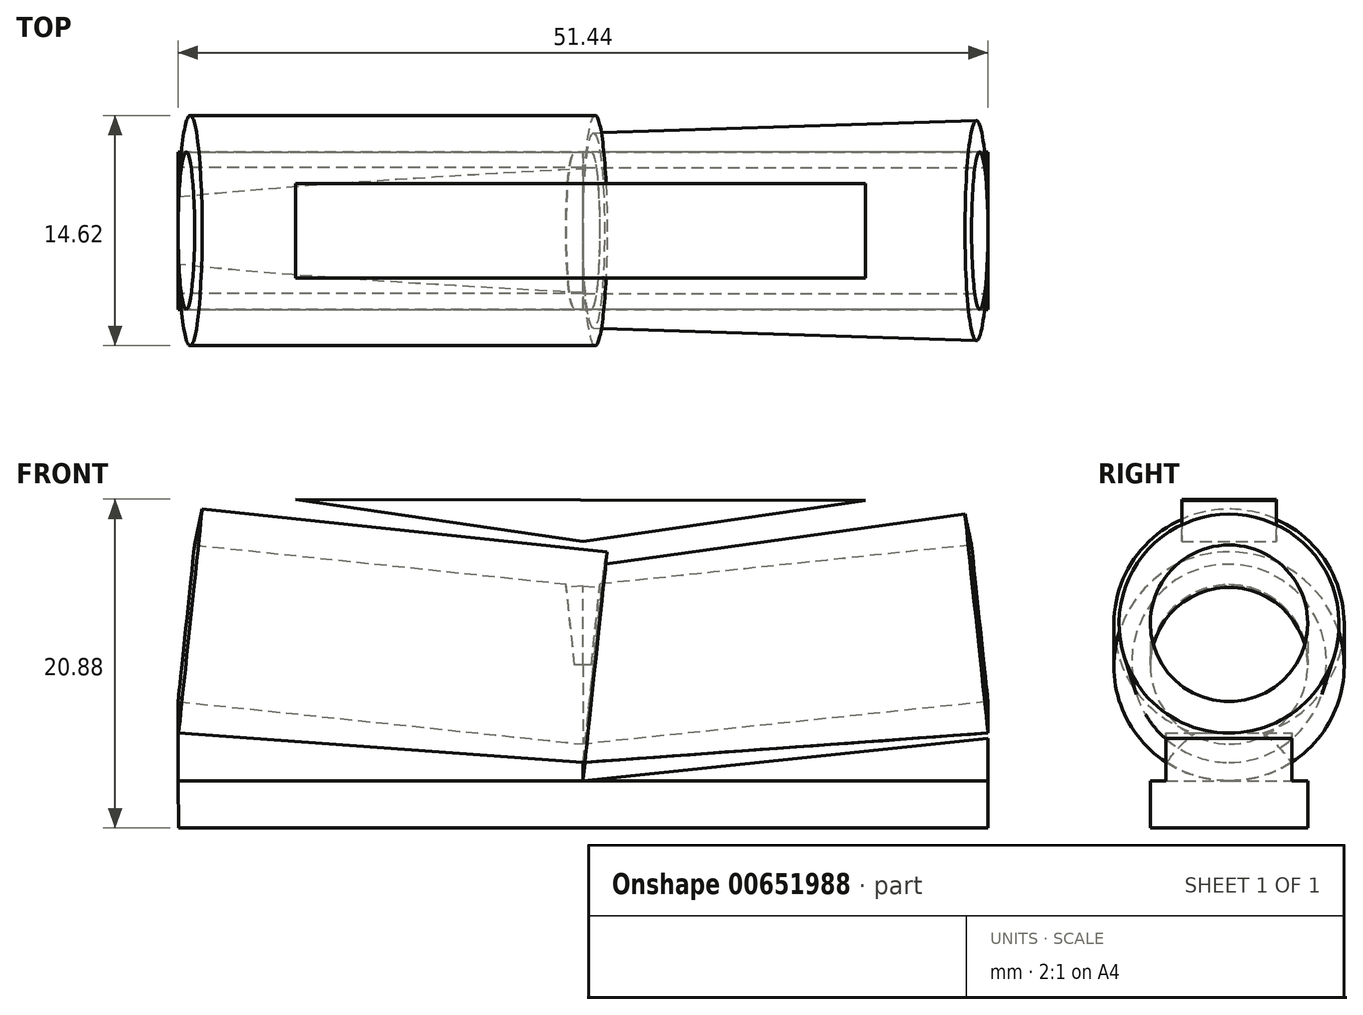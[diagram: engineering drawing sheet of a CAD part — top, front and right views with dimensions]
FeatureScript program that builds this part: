
annotation { "Feature Type Name" : "Feature", "Feature Type Description" : "" }
export const myFeature = defineFeature(function(context is Context, id is Id, definition is map)
    precondition{}
    {
        {
            var Q0;
            Q0=qCreatedBy(makeId("Front.planeOp"),FACE);
            var sketch = newSketch(context, id + "F0", { "sketchPlane" : qUnion([Q0])});
            skLineSegment(sketch, "E0", {"start": v(0, 0) * mm, "end": v(25.72, 0) * mm});
            skLineSegment(sketch, "E1", {"start": v(0, 0) * mm, "end": v(25.72, 2.7) * mm});
            skLineSegment(sketch, "E2", {"start": v(25.72, 2.7) * mm, "end": v(0, 0) * mm});
            skLineSegment(sketch, "E3", {"start": v(0, 2.32) * mm, "end": v(25.72, 5.03) * mm});
            skLineSegment(sketch, "E4", {"start": v(0, 0) * mm, "end": v(0, 2.32) * mm});
            skLineSegment(sketch, "E5", {"start": v(0, 7.35) * mm, "end": v(25.72, 10.06) * mm});
            skLineSegment(sketch, "E6", {"start": v(0, 2.32) * mm, "end": v(0, 7.35) * mm});
            skPoint(sketch, "E7", {"position": v(0, 2.32) * mm});
            skLineSegment(sketch, "E8", {"start": v(25.72, 10.06) * mm, "end": v(25.72, 0) * mm});
            skPoint(sketch, "E9", {"position": v(0, 0) * mm});
            skLineSegment(sketch, "E10.MirrorCS", {"start": v(0, 7.35) * mm, "end": v(-25.72, 10.06) * mm});
            skLineSegment(sketch, "E11.MirrorCS", {"start": v(0, 2.32) * mm, "end": v(-25.72, 5.03) * mm});
            skLineSegment(sketch, "E12.MirrorCS", {"start": v(-25.72, 2.7) * mm, "end": v(0, 0) * mm});
            skLineSegment(sketch, "E13.MirrorCS", {"start": v(0, 0) * mm, "end": v(-25.72, 0) * mm});
            skLineSegment(sketch, "E14.MirrorCS", {"start": v(-25.72, 10.06) * mm, "end": v(-25.72, 0) * mm});
            skLineSegment(sketch, "E15", {"start": v(25.72, 0) * mm, "end": v(25.72, -3) * mm});
            skLineSegment(sketch, "E16", {"start": v(25.72, -3) * mm, "end": v(-25.7, -3) * mm});
            skLineSegment(sketch, "E17", {"start": v(-25.7, -3) * mm, "end": v(-25.72, 0) * mm});
            skPoint(sketch, "E18", {"position": v(-25.72, 5.03) * mm});
            skPoint(sketch, "E19", {"position": v(-25.72, 2.7) * mm});
            skPoint(sketch, "E20", {"position": v(-25.72, 0) * mm});
            skPoint(sketch, "E21", {"position": v(25.72, 0) * mm});
            skPoint(sketch, "E22", {"position": v(25.72, 2.7) * mm});
            skPoint(sketch, "E23", {"position": v(25.72, 5.03) * mm});
            skPoint(sketch, "E24", {"position": v(0, 1.16) * mm});
            skPoint(sketch, "E25", {"position": v(-25.72, 3.03) * mm});
            skLineSegment(sketch, "E26", {"start": v(0, 1.16) * mm, "end": v(-25.72, 3.03) * mm});
            skPoint(sketch, "E27", {"position": v(25.72, 3.03) * mm});
            skLineSegment(sketch, "E28", {"start": v(25.72, 3.03) * mm, "end": v(0, 1.16) * mm});
            skSolve(sketch);
        }
        {
            var Q0;
            {var subQ0=sQuery(id+"F0.wireOp",EDGE,"E11.MirrorCS");Q0=makeQuery(id+"F0.imprint","IMPRINT",FACE,{"disambiguationData":[TD([[makeQuery(id+"F0.imprint","IMPRINT",EDGE,{"derivedFrom":subQ0}),1.0]])]});}
            var Q1;
            {var subQ0=sQuery(id+"F0.wireOp",EDGE,"E12.MirrorCS");Q1=makeQuery(id+"F0.imprint","IMPRINT",FACE,{"disambiguationData":[TD([[makeQuery(id+"F0.imprint","IMPRINT",EDGE,{"derivedFrom":subQ0}),1.0]])]});}
            var Q2;
            Q2=sQuery(id+"F0.wireOp",EDGE,"E10.MirrorCS");
            revolve(context, id + "F1", {"entities" : qUnion([Q0, Q1]), "axis" : qUnion([Q2]), "revolveType" : RevolveType.FULL});
        }
        {
            var Q0;
            {var subQ0=sQuery(id+"F0.wireOp",EDGE,"E2");Q0=makeQuery(id+"F0.imprint","IMPRINT",FACE,{"disambiguationData":[TD([[makeQuery(id+"F0.imprint","IMPRINT",EDGE,{"derivedFrom":subQ0}),-1.0]])]});}
            var Q1;
            {var subQ0=sQuery(id+"F0.wireOp",EDGE,"E3");Q1=makeQuery(id+"F0.imprint","IMPRINT",FACE,{"disambiguationData":[TD([[makeQuery(id+"F0.imprint","IMPRINT",EDGE,{"derivedFrom":subQ0}),-1.0]])]});}
            var Q2;
            Q2=sQuery(id+"F0.wireOp",EDGE,"E5");
            revolve(context, id + "F2", {"operationType" : NewBodyOperationType.ADD, "entities" : qUnion([Q0, Q1]), "axis" : qUnion([Q2]), "revolveType" : RevolveType.FULL});
        }
        {
            var Q0;
            Q0=qCreatedBy(makeId("Front.planeOp"),FACE);
            var sketch = newSketch(context, id + "F3", { "sketchPlane" : qUnion([Q0])});
            skPoint(sketch, "E29", {"position": v(0, 15.2) * mm});
            skPoint(sketch, "E30", {"position": v(17.94, 17.8) * mm});
            skPoint(sketch, "E31", {"position": v(-18.27, 17.88) * mm});
            skLineSegment(sketch, "E32", {"start": v(-18.27, 17.88) * mm, "end": v(0, 15.2) * mm});
            skLineSegment(sketch, "E33", {"start": v(17.94, 17.8) * mm, "end": v(-18.27, 17.88) * mm});
            skLineSegment(sketch, "E34", {"start": v(0, 15.2) * mm, "end": v(17.94, 17.8) * mm});
            skSolve(sketch);
        }
        {
            var Q0;
            Q0=makeQuery(id+"F3.imprint","IMPRINT",FACE,{"disambiguationData":[TD([[makeQuery(id+"F3.imprint","IMPRINT",EDGE,{"derivedFrom":sQuery(id+"F3.wireOp",EDGE,"E32")}),1.0]])]});
            extrude(context, id + "F4", {"entities" : qUnion([Q0]), "operationType" : NewBodyOperationType.ADD, "endBound" : BoundingType.SYMMETRIC, "depth" : 6 * mm, "offsetDistance" : 25 * mm});
        }
        {
            var Q0;
            Q0=makeQuery(id+"F0.imprint","IMPRINT",FACE,{"disambiguationData":[TD([[makeQuery(id+"F0.imprint","IMPRINT",EDGE,{"derivedFrom":sQuery(id+"F0.wireOp",EDGE,"E0")}),-1.0]])]});
            extrude(context, id + "F5", {"entities" : qUnion([Q0]), "endBound" : BoundingType.SYMMETRIC, "depth" : 10 * mm, "offsetDistance" : 25 * mm});
        }
        {
            var Q0;
            {var subQ0=sQuery(id+"F0.wireOp",EDGE,"E12.MirrorCS");Q0=makeQuery(id+"F0.imprint","IMPRINT",FACE,{"disambiguationData":[TD([[makeQuery(id+"F0.imprint","IMPRINT",EDGE,{"derivedFrom":subQ0}),-1.0]])]});}
            var Q1;
            {var subQ0=sQuery(id+"F0.wireOp",EDGE,"E0");Q1=makeQuery(id+"F0.imprint","IMPRINT",FACE,{"disambiguationData":[TD([[makeQuery(id+"F0.imprint","IMPRINT",EDGE,{"derivedFrom":subQ0}),1.0]])]});}
            var Q2;
            {var subQ0=sQuery(id+"F0.wireOp",EDGE,"E12.MirrorCS");Q2=makeQuery(id+"F0.imprint","IMPRINT",FACE,{"disambiguationData":[TD([[makeQuery(id+"F0.imprint","IMPRINT",EDGE,{"derivedFrom":subQ0}),1.0]])]});}
            var Q3;
            {var subQ0=sQuery(id+"F0.wireOp",EDGE,"E2");Q3=makeQuery(id+"F0.imprint","IMPRINT",FACE,{"disambiguationData":[TD([[makeQuery(id+"F0.imprint","IMPRINT",EDGE,{"derivedFrom":subQ0}),-1.0]])]});}
            extrude(context, id + "F6", {"entities" : qUnion([Q0, Q1, Q2, Q3]), "operationType" : NewBodyOperationType.ADD, "endBound" : BoundingType.SYMMETRIC, "depth" : 8 * mm, "offsetDistance" : 25 * mm});
        }
    });
